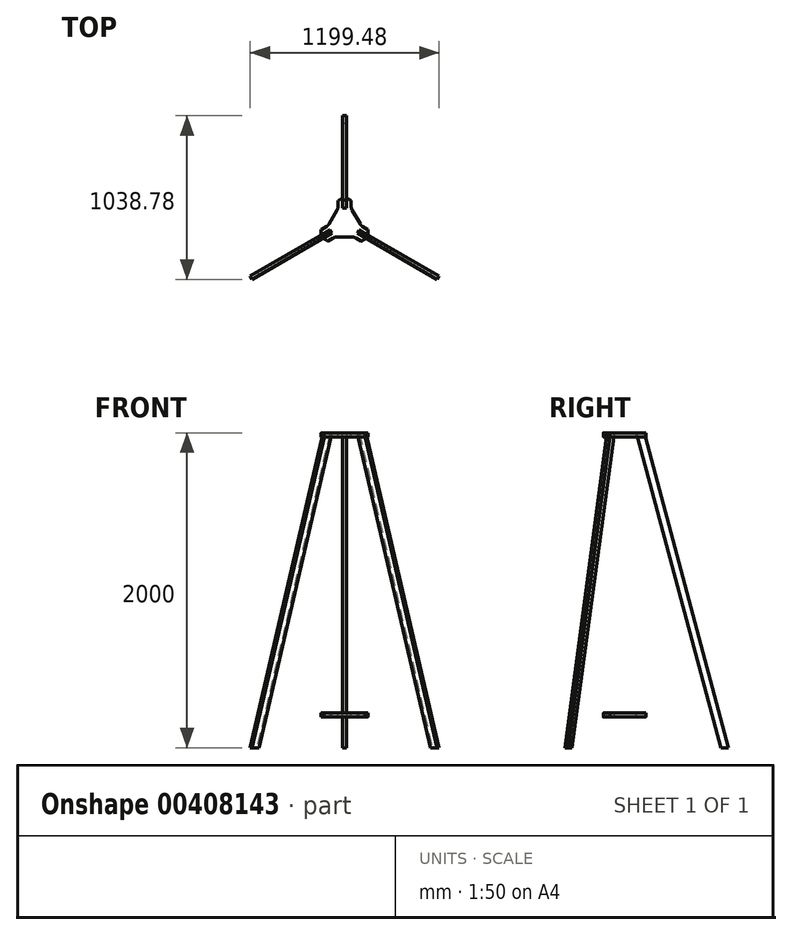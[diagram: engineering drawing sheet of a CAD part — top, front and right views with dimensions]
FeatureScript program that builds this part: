
annotation { "Feature Type Name" : "Feature", "Feature Type Description" : "" }
export const myFeature = defineFeature(function(context is Context, id is Id, definition is map)
    precondition{}
    {
        {
            var Q0;
            Q0=qCreatedBy(makeId("Right.planeOp"),FACE);
            var sketch = newSketch(context, id + "F0", { "sketchPlane" : qUnion([Q0])});
            skLineSegment(sketch, "E0", {"start": v(100, 2000) * mm, "end": v(635.9, 0) * mm});
            skLineSegment(sketch, "E1", {"start": v(635.9, 0) * mm, "end": v(685.6, 0) * mm});
            skLineSegment(sketch, "E2", {"start": v(685.6, 0) * mm, "end": v(149.7, 2000) * mm});
            skLineSegment(sketch, "E3", {"start": v(149.7, 2000) * mm, "end": v(100, 2000) * mm});
            skLineSegment(sketch, "E4", {"start": v(0, 701.56) * mm, "end": v(0, -60.84) * mm, "construction": true});
            skSolve(sketch);
        }
        {
            var Q0;
            Q0=makeQuery(id+"F0.imprint","IMPRINT",FACE,{"disambiguationData":[TD([[makeQuery(id+"F0.imprint","IMPRINT",EDGE,{"derivedFrom":sQuery(id+"F0.wireOp",EDGE,"E0")}),1.0]])]});
            extrude(context, id + "F1", {"entities" : qUnion([Q0]), "endBound" : BoundingType.SYMMETRIC, "depth" : 24 * mm});
        }
        {
            var Q0;
            Q0=makeQuery(id+"F1.opExtrude","SWEPT_BODY",BODY,{"disambiguationData":[OSD([sQuery(id+"F0.wireOp",EDGE,"E0"),sQuery(id+"F0.wireOp",EDGE,"E1"),sQuery(id+"F0.wireOp",EDGE,"E2"),sQuery(id+"F0.wireOp",EDGE,"E3")])]});
            var Q1;
            Q1=sQuery(id+"F0.wireOp",EDGE,"E4");
            circularPattern(context, id + "F2", {"entities" : qUnion([Q0]), "axis" : qUnion([Q1]), "angle" : 360 * degree, "instanceCount" : 3, "equalSpace" : true});
        }
        {
            var Q0;
            Q0=makeQuery(id+"F2.opPattern","COPY",FACE,{"derivedFrom":makeQuery(id+"F1.opExtrude","SWEPT_FACE",FACE,{"disambiguationData":[OSD([sQuery(id+"F0.wireOp",EDGE,"E3")])]}),"instanceName":"1"});
            var sketch = newSketch(context, id + "F3", { "sketchPlane" : qUnion([Q0])});
            skLineSegment(sketch, "E5", {"start": v(-166.53, -110) * mm, "end": v(-106.53, -110) * mm});
            skLineSegment(sketch, "E6", {"start": v(178.53, -89.22) * mm, "end": v(148.53, -37.25) * mm});
            skLineSegment(sketch, "E7", {"start": v(-12, 199.22) * mm, "end": v(-42, 147.25) * mm});
            skLineSegment(sketch, "E8", {"start": v(166.53, -110) * mm, "end": v(80.6, -60.4) * mm});
            skLineSegment(sketch, "E9", {"start": v(80.6, -60.4) * mm, "end": v(92.6, -39.6) * mm});
            skLineSegment(sketch, "E10", {"start": v(92.6, -39.6) * mm, "end": v(178.53, -89.22) * mm});
            skLineSegment(sketch, "E11", {"start": v(-12, 199.22) * mm, "end": v(-12, 100) * mm});
            skLineSegment(sketch, "E12", {"start": v(-12, 100) * mm, "end": v(12, 100) * mm});
            skLineSegment(sketch, "E13", {"start": v(12, 100) * mm, "end": v(12, 199.22) * mm});
            skPoint(sketch, "E14.orphan", {"position": v(0, 220) * mm});
            skLineSegment(sketch, "E15", {"start": v(-166.53, -110) * mm, "end": v(-80.6, -60.4) * mm});
            skLineSegment(sketch, "E16", {"start": v(-80.6, -60.4) * mm, "end": v(-92.6, -39.6) * mm});
            skLineSegment(sketch, "E17", {"start": v(-92.6, -39.6) * mm, "end": v(-178.53, -89.22) * mm});
            skPoint(sketch, "E18.orphan", {"position": v(-190.53, -110) * mm});
            skLineSegment(sketch, "E19", {"start": v(-106.53, -110) * mm, "end": v(-63.22, -85) * mm});
            skLineSegment(sketch, "E20", {"start": v(-63.22, -85) * mm, "end": v(63.22, -85) * mm});
            skLineSegment(sketch, "E21", {"start": v(63.22, -85) * mm, "end": v(106.53, -110) * mm});
            skLineSegment(sketch, "E22.1.0", {"start": v(148.53, -37.25) * mm, "end": v(105.22, -12.25) * mm});
            skLineSegment(sketch, "E22.1.1", {"start": v(105.22, -12.25) * mm, "end": v(42, 97.25) * mm});
            skLineSegment(sketch, "E22.1.2", {"start": v(42, 97.25) * mm, "end": v(42, 147.25) * mm});
            skLineSegment(sketch, "E22.2.0", {"start": v(-42, 147.25) * mm, "end": v(-42, 97.25) * mm});
            skLineSegment(sketch, "E22.2.1", {"start": v(-42, 97.25) * mm, "end": v(-105.22, -12.25) * mm});
            skLineSegment(sketch, "E22.2.2", {"start": v(-105.22, -12.25) * mm, "end": v(-148.53, -37.25) * mm});
            skPoint(sketch, "E22.center", {"position": v(0, 0) * mm});
            skLineSegment(sketch, "E23.trimOffspring", {"start": v(106.53, -110) * mm, "end": v(166.53, -110) * mm});
            skLineSegment(sketch, "E24.trimOffspring", {"start": v(-148.53, -37.25) * mm, "end": v(-178.53, -89.22) * mm});
            skLineSegment(sketch, "E25.trimOffspring", {"start": v(42, 147.25) * mm, "end": v(12, 199.22) * mm});
            skSolve(sketch);
        }
        {
            var Q0;
            Q0 = qSketchRegion(id + "F3", true);
            extrude(context, id + "F4", {"entities" : qUnion([Q0]), "oppositeDirection" : true, "depth" : 25 * mm});
        }
        {
            var Q0;
            Q0=makeQuery(id+"F4.opExtrude","SWEPT_EDGE",EDGE,{"disambiguationData":[OSD([sQuery(id+"F3.wireOp",EDGE,"E5"),sQuery(id+"F3.wireOp",EDGE,"E15")])]});
            var Q1;
            Q1=makeQuery(id+"F4.opExtrude","SWEPT_EDGE",EDGE,{"disambiguationData":[OSD([sQuery(id+"F3.wireOp",EDGE,"E6"),sQuery(id+"F3.wireOp",EDGE,"E10")])]});
            var Q2;
            Q2=makeQuery(id+"F4.opExtrude","SWEPT_EDGE",EDGE,{"disambiguationData":[OSD([sQuery(id+"F3.wireOp",EDGE,"E7"),sQuery(id+"F3.wireOp",EDGE,"E11")])]});
            chamfer(context, id + "F5", {"entities" : qUnion([Q0, Q1, Q2]), "chamferType" : ChamferType.TWO_OFFSETS, "width1" : 35 * mm, "oppositeDirection" : false, "width2" : 60 * mm});
        }
        {
            var Q0;
            Q0=makeQuery(id+"F4.opExtrude","SWEPT_EDGE",EDGE,{"disambiguationData":[OSD([sQuery(id+"F3.wireOp",EDGE,"E13"),sQuery(id+"F3.wireOp",EDGE,"E25.trimOffspring")])]});
            var Q1;
            Q1=makeQuery(id+"F4.opExtrude","SWEPT_EDGE",EDGE,{"disambiguationData":[OSD([sQuery(id+"F3.wireOp",EDGE,"E8"),sQuery(id+"F3.wireOp",EDGE,"E23.trimOffspring")])]});
            var Q2;
            Q2=makeQuery(id+"F4.opExtrude","SWEPT_EDGE",EDGE,{"disambiguationData":[OSD([sQuery(id+"F3.wireOp",EDGE,"E17"),sQuery(id+"F3.wireOp",EDGE,"E24.trimOffspring")])]});
            chamfer(context, id + "F6", {"entities" : qUnion([Q0, Q1, Q2]), "chamferType" : ChamferType.TWO_OFFSETS, "width1" : 60 * mm, "oppositeDirection" : false, "width2" : 35 * mm, "tangentPropagation" : true});
        }
        {
            var Q0;
            {var subQ0=sQuery(id+"F3.wireOp",EDGE,"E17");Q0=makeQuery(id+"F6.opChamfer","BLEND_EDGE",EDGE,{"blendedFrom":[makeQuery(id+"F4.opExtrude","SWEPT_EDGE",EDGE,{"disambiguationData":[OSD([subQ0,sQuery(id+"F3.wireOp",EDGE,"E24.trimOffspring")])]}),makeQuery(id+"F4.opExtrude","SWEPT_FACE",FACE,{"disambiguationData":[OSD([subQ0])]})],"blendedInto":[makeQuery(id+"F4.opExtrude","SWEPT_FACE",FACE,{"disambiguationData":[OSD([subQ0])]})]});}
            var Q1;
            {var subQ0=sQuery(id+"F3.wireOp",EDGE,"E15");Q1=makeQuery(id+"F5.opChamfer","BLEND_EDGE",EDGE,{"blendedFrom":[makeQuery(id+"F4.opExtrude","SWEPT_EDGE",EDGE,{"disambiguationData":[OSD([sQuery(id+"F3.wireOp",EDGE,"E5"),subQ0])]}),makeQuery(id+"F4.opExtrude","SWEPT_FACE",FACE,{"disambiguationData":[OSD([subQ0])]})],"blendedInto":[makeQuery(id+"F4.opExtrude","SWEPT_FACE",FACE,{"disambiguationData":[OSD([subQ0])]})]});}
            var Q2;
            Q2=makeQuery(id+"F5.opChamfer","BLEND_EDGE",EDGE,{"blendedFrom":[makeQuery(id+"F4.opExtrude","SWEPT_EDGE",EDGE,{"disambiguationData":[OSD([sQuery(id+"F3.wireOp",EDGE,"E5"),sQuery(id+"F3.wireOp",EDGE,"E15")])]}),makeQuery(id+"F4.opExtrude","SWEPT_FACE",FACE,{"disambiguationData":[OSD([sQuery(id+"F3.wireOp",EDGE,"E19")])]})],"blendedInto":[makeQuery(id+"F4.opExtrude","SWEPT_FACE",FACE,{"disambiguationData":[OSD([sQuery(id+"F3.wireOp",EDGE,"E19")])]})]});
            var Q3;
            Q3=makeQuery(id+"F6.opChamfer","BLEND_EDGE",EDGE,{"blendedFrom":[makeQuery(id+"F4.opExtrude","SWEPT_EDGE",EDGE,{"disambiguationData":[OSD([sQuery(id+"F3.wireOp",EDGE,"E17"),sQuery(id+"F3.wireOp",EDGE,"E24.trimOffspring")])]}),makeQuery(id+"F4.opExtrude","SWEPT_FACE",FACE,{"disambiguationData":[OSD([sQuery(id+"F3.wireOp",EDGE,"E22.2.2")])]})],"blendedInto":[makeQuery(id+"F4.opExtrude","SWEPT_FACE",FACE,{"disambiguationData":[OSD([sQuery(id+"F3.wireOp",EDGE,"E22.2.2")])]})]});
            var Q4;
            Q4=makeQuery(id+"F5.opChamfer","BLEND_EDGE",EDGE,{"blendedFrom":[makeQuery(id+"F4.opExtrude","SWEPT_EDGE",EDGE,{"disambiguationData":[OSD([sQuery(id+"F3.wireOp",EDGE,"E7"),sQuery(id+"F3.wireOp",EDGE,"E11")])]}),makeQuery(id+"F4.opExtrude","SWEPT_FACE",FACE,{"disambiguationData":[OSD([sQuery(id+"F3.wireOp",EDGE,"E22.2.0")])]})],"blendedInto":[makeQuery(id+"F4.opExtrude","SWEPT_FACE",FACE,{"disambiguationData":[OSD([sQuery(id+"F3.wireOp",EDGE,"E22.2.0")])]})]});
            var Q5;
            {var subQ0=sQuery(id+"F3.wireOp",EDGE,"E11");Q5=makeQuery(id+"F5.opChamfer","BLEND_EDGE",EDGE,{"blendedFrom":[makeQuery(id+"F4.opExtrude","SWEPT_EDGE",EDGE,{"disambiguationData":[OSD([sQuery(id+"F3.wireOp",EDGE,"E7"),subQ0])]}),makeQuery(id+"F4.opExtrude","SWEPT_FACE",FACE,{"disambiguationData":[OSD([subQ0])]})],"blendedInto":[makeQuery(id+"F4.opExtrude","SWEPT_FACE",FACE,{"disambiguationData":[OSD([subQ0])]})]});}
            var Q6;
            {var subQ0=sQuery(id+"F3.wireOp",EDGE,"E13");Q6=makeQuery(id+"F6.opChamfer","BLEND_EDGE",EDGE,{"blendedFrom":[makeQuery(id+"F4.opExtrude","SWEPT_EDGE",EDGE,{"disambiguationData":[OSD([subQ0,sQuery(id+"F3.wireOp",EDGE,"E25.trimOffspring")])]}),makeQuery(id+"F4.opExtrude","SWEPT_FACE",FACE,{"disambiguationData":[OSD([subQ0])]})],"blendedInto":[makeQuery(id+"F4.opExtrude","SWEPT_FACE",FACE,{"disambiguationData":[OSD([subQ0])]})]});}
            var Q7;
            Q7=makeQuery(id+"F6.opChamfer","BLEND_EDGE",EDGE,{"blendedFrom":[makeQuery(id+"F4.opExtrude","SWEPT_EDGE",EDGE,{"disambiguationData":[OSD([sQuery(id+"F3.wireOp",EDGE,"E13"),sQuery(id+"F3.wireOp",EDGE,"E25.trimOffspring")])]}),makeQuery(id+"F4.opExtrude","SWEPT_FACE",FACE,{"disambiguationData":[OSD([sQuery(id+"F3.wireOp",EDGE,"E22.1.2")])]})],"blendedInto":[makeQuery(id+"F4.opExtrude","SWEPT_FACE",FACE,{"disambiguationData":[OSD([sQuery(id+"F3.wireOp",EDGE,"E22.1.2")])]})]});
            var Q8;
            Q8=makeQuery(id+"F5.opChamfer","BLEND_EDGE",EDGE,{"blendedFrom":[makeQuery(id+"F4.opExtrude","SWEPT_EDGE",EDGE,{"disambiguationData":[OSD([sQuery(id+"F3.wireOp",EDGE,"E6"),sQuery(id+"F3.wireOp",EDGE,"E10")])]}),makeQuery(id+"F4.opExtrude","SWEPT_FACE",FACE,{"disambiguationData":[OSD([sQuery(id+"F3.wireOp",EDGE,"E22.1.0")])]})],"blendedInto":[makeQuery(id+"F4.opExtrude","SWEPT_FACE",FACE,{"disambiguationData":[OSD([sQuery(id+"F3.wireOp",EDGE,"E22.1.0")])]})]});
            var Q9;
            {var subQ0=sQuery(id+"F3.wireOp",EDGE,"E10");Q9=makeQuery(id+"F5.opChamfer","BLEND_EDGE",EDGE,{"blendedFrom":[makeQuery(id+"F4.opExtrude","SWEPT_EDGE",EDGE,{"disambiguationData":[OSD([sQuery(id+"F3.wireOp",EDGE,"E6"),subQ0])]}),makeQuery(id+"F4.opExtrude","SWEPT_FACE",FACE,{"disambiguationData":[OSD([subQ0])]})],"blendedInto":[makeQuery(id+"F4.opExtrude","SWEPT_FACE",FACE,{"disambiguationData":[OSD([subQ0])]})]});}
            var Q10;
            {var subQ0=sQuery(id+"F3.wireOp",EDGE,"E8");Q10=makeQuery(id+"F6.opChamfer","BLEND_EDGE",EDGE,{"blendedFrom":[makeQuery(id+"F4.opExtrude","SWEPT_EDGE",EDGE,{"disambiguationData":[OSD([subQ0,sQuery(id+"F3.wireOp",EDGE,"E23.trimOffspring")])]}),makeQuery(id+"F4.opExtrude","SWEPT_FACE",FACE,{"disambiguationData":[OSD([subQ0])]})],"blendedInto":[makeQuery(id+"F4.opExtrude","SWEPT_FACE",FACE,{"disambiguationData":[OSD([subQ0])]})]});}
            var Q11;
            Q11=makeQuery(id+"F6.opChamfer","BLEND_EDGE",EDGE,{"blendedFrom":[makeQuery(id+"F4.opExtrude","SWEPT_EDGE",EDGE,{"disambiguationData":[OSD([sQuery(id+"F3.wireOp",EDGE,"E8"),sQuery(id+"F3.wireOp",EDGE,"E23.trimOffspring")])]}),makeQuery(id+"F4.opExtrude","SWEPT_FACE",FACE,{"disambiguationData":[OSD([sQuery(id+"F3.wireOp",EDGE,"E21")])]})],"blendedInto":[makeQuery(id+"F4.opExtrude","SWEPT_FACE",FACE,{"disambiguationData":[OSD([sQuery(id+"F3.wireOp",EDGE,"E21")])]})]});
            fillet(context, id + "F7", {"entities" : qUnion([Q0, Q1, Q2, Q3, Q4, Q5, Q6, Q7, Q8, Q9, Q10, Q11]), "radius" : 5 * mm, "tangentPropagation" : true, "allowEdgeOverflow" : false});
        }
        {
            var Q0;
            Q0=makeQuery(id+"F4.opExtrude","SWEPT_EDGE",EDGE,{"disambiguationData":[OSD([sQuery(id+"F3.wireOp",EDGE,"E22.2.0"),sQuery(id+"F3.wireOp",EDGE,"E22.2.1")])]});
            var Q1;
            Q1=makeQuery(id+"F4.opExtrude","SWEPT_EDGE",EDGE,{"disambiguationData":[OSD([sQuery(id+"F3.wireOp",EDGE,"E22.2.1"),sQuery(id+"F3.wireOp",EDGE,"E22.2.2")])]});
            var Q2;
            Q2=makeQuery(id+"F4.opExtrude","SWEPT_EDGE",EDGE,{"disambiguationData":[OSD([sQuery(id+"F3.wireOp",EDGE,"E19"),sQuery(id+"F3.wireOp",EDGE,"E20")])]});
            var Q3;
            Q3=makeQuery(id+"F4.opExtrude","SWEPT_EDGE",EDGE,{"disambiguationData":[OSD([sQuery(id+"F3.wireOp",EDGE,"E20"),sQuery(id+"F3.wireOp",EDGE,"E21")])]});
            var Q4;
            Q4=makeQuery(id+"F4.opExtrude","SWEPT_EDGE",EDGE,{"disambiguationData":[OSD([sQuery(id+"F3.wireOp",EDGE,"E22.1.0"),sQuery(id+"F3.wireOp",EDGE,"E22.1.1")])]});
            var Q5;
            Q5=makeQuery(id+"F4.opExtrude","SWEPT_EDGE",EDGE,{"disambiguationData":[OSD([sQuery(id+"F3.wireOp",EDGE,"E22.1.1"),sQuery(id+"F3.wireOp",EDGE,"E22.1.2")])]});
            fillet(context, id + "F8", {"entities" : qUnion([Q0, Q1, Q2, Q3, Q4, Q5]), "radius" : 40 * mm, "tangentPropagation" : true, "allowEdgeOverflow" : false});
        }
        {
            var Q0;
            Q0=makeQuery(id+"F4.opExtrude","SWEPT_BODY",BODY,{"disambiguationData":[OSD([sQuery(id+"F3.wireOp",EDGE,"E5"),sQuery(id+"F3.wireOp",EDGE,"E6"),sQuery(id+"F3.wireOp",EDGE,"E7"),sQuery(id+"F3.wireOp",EDGE,"E8"),sQuery(id+"F3.wireOp",EDGE,"E9"),sQuery(id+"F3.wireOp",EDGE,"E10"),sQuery(id+"F3.wireOp",EDGE,"E11"),sQuery(id+"F3.wireOp",EDGE,"E12"),sQuery(id+"F3.wireOp",EDGE,"E13"),sQuery(id+"F3.wireOp",EDGE,"E15"),sQuery(id+"F3.wireOp",EDGE,"E16"),sQuery(id+"F3.wireOp",EDGE,"E17"),sQuery(id+"F3.wireOp",EDGE,"E19"),sQuery(id+"F3.wireOp",EDGE,"E20"),sQuery(id+"F3.wireOp",EDGE,"E21"),sQuery(id+"F3.wireOp",EDGE,"E22.1.0"),sQuery(id+"F3.wireOp",EDGE,"E22.1.1"),sQuery(id+"F3.wireOp",EDGE,"E22.1.2"),sQuery(id+"F3.wireOp",EDGE,"E22.2.0"),sQuery(id+"F3.wireOp",EDGE,"E22.2.1"),sQuery(id+"F3.wireOp",EDGE,"E22.2.2"),sQuery(id+"F3.wireOp",EDGE,"E23.trimOffspring"),sQuery(id+"F3.wireOp",EDGE,"E24.trimOffspring"),sQuery(id+"F3.wireOp",EDGE,"E25.trimOffspring")])]});
            transform(context, id + "F9", {"entities" : qUnion([Q0]), "transformType" : TransformType.TRANSLATION_3D, "dx" : 0 * mm, "dy" : 0 * mm, "dz" : -1780 * mm, "makeCopy" : true});
        }
    });
